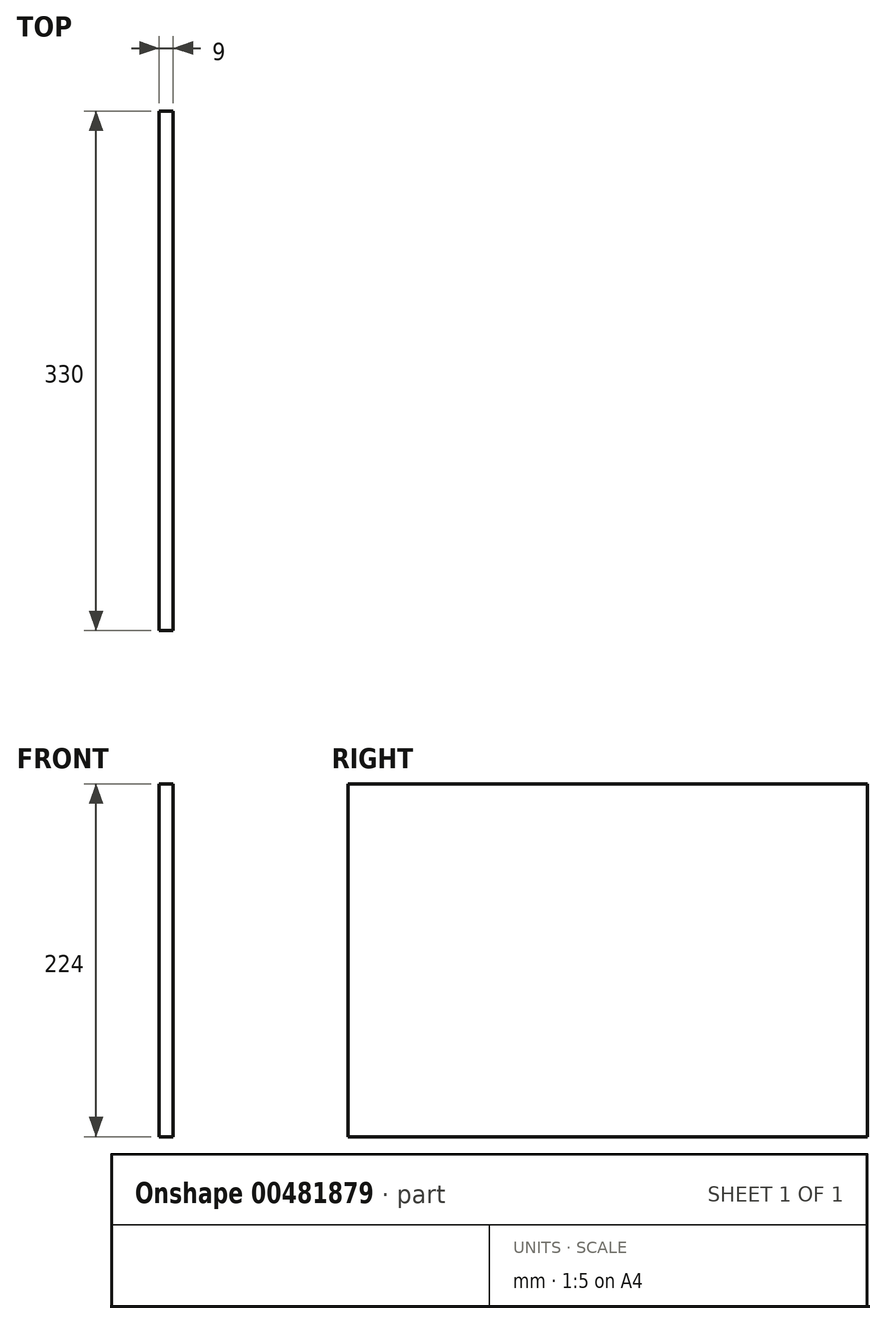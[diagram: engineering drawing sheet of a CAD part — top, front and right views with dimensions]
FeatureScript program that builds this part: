
annotation { "Feature Type Name" : "Feature", "Feature Type Description" : "" }
export const myFeature = defineFeature(function(context is Context, id is Id, definition is map)
    precondition{}
    {
        {
            var Q0;
            Q0=qCreatedBy(makeId("Right.planeOp"),FACE);
            var sketch = newSketch(context, id + "F0", { "sketchPlane" : qUnion([Q0])});
            skLineSegment(sketch, "E0.bottom", {"start": v(0, 0) * mm, "end": v(330, 0) * mm});
            skLineSegment(sketch, "E0.top", {"start": v(0, 224) * mm, "end": v(330, 224) * mm});
            skLineSegment(sketch, "E0.left", {"start": v(0, 0) * mm, "end": v(0, 224) * mm});
            skLineSegment(sketch, "E0.right", {"start": v(330, 0) * mm, "end": v(330, 224) * mm});
            skSolve(sketch);
        }
        {
            var Q0;
            Q0 = qSketchRegion(id + "F0", true);
            extrude(context, id + "F1", {"entities" : qUnion([Q0]), "depth" : 9 * mm});
        }
    });
